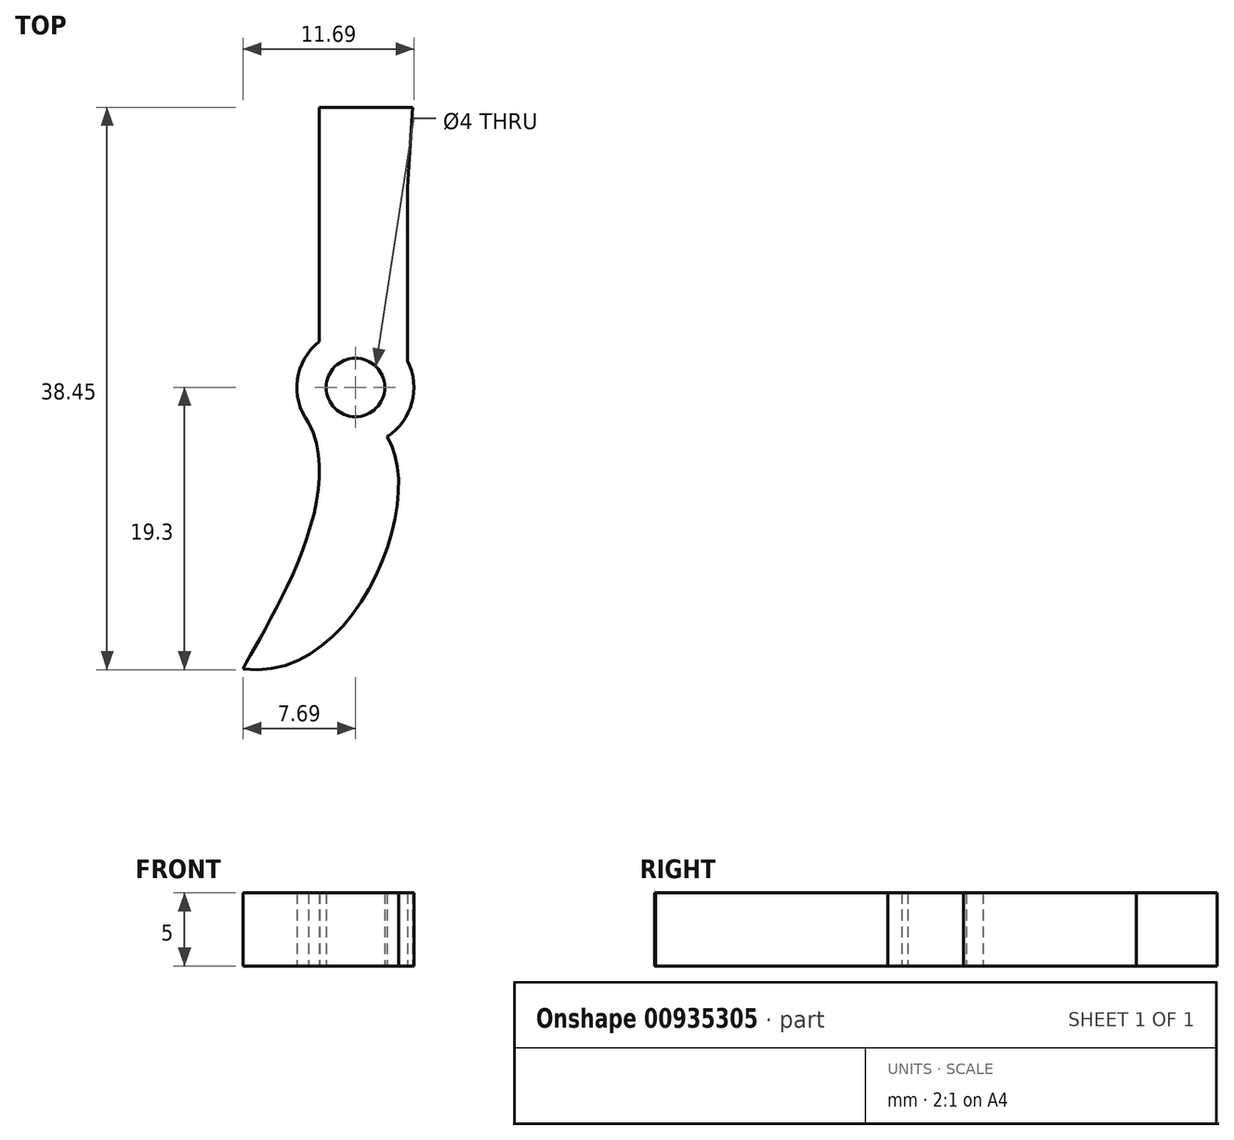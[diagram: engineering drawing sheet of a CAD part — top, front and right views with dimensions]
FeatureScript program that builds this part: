
annotation { "Feature Type Name" : "Feature", "Feature Type Description" : "" }
export const myFeature = defineFeature(function(context is Context, id is Id, definition is map)
    precondition{}
    {
        {
            var Q0;
            Q0=qCreatedBy(makeId("Top.planeOp"),FACE);
            var sketch = newSketch(context, id + "F0", { "sketchPlane" : qUnion([Q0])});
            skCircle(sketch, "E0", {"center": v(0, 0) * mm, "radius": 2 * mm});
            skCircle(sketch, "E1.0", {"center": v(0, 0) * mm, "radius": 4 * mm});
            skFitSpline(sketch, "E2", {"points": [v(-3.58, -1.78) * mm, v(-7.69, -19.23) * mm], "startDerivative": vector(10.75, -15.19) * mm, "endDerivative": vector(-5.28, -9.9) * mm});
            skFitSpline(sketch, "E3", {"points": [v(-7.69, -19.23) * mm, v(2.15, -3.37) * mm], "startDerivative": vector(23.06, -3.24) * mm, "endDerivative": vector(-8.43, 12.87) * mm});
            skLineSegment(sketch, "E4", {"start": v(-2.46, 3.15) * mm, "end": v(-2.46, 13.64) * mm});
            skLineSegment(sketch, "E5", {"start": v(3.57, 13.64) * mm, "end": v(3.57, 1.8) * mm});
            skLineSegment(sketch, "E6", {"start": v(-2.46, 13.64) * mm, "end": v(-2.46, 19.15) * mm});
            skLineSegment(sketch, "E7", {"start": v(-2.46, 19.15) * mm, "end": v(3.9, 19.15) * mm});
            skLineSegment(sketch, "E8", {"start": v(3.9, 19.15) * mm, "end": v(3.57, 13.64) * mm});
            skSolve(sketch);
        }
        {
            var Q0;
            Q0 = qSketchRegion(id + "F0", true);
            extrude(context, id + "F1", {"entities" : qUnion([Q0]), "depth" : 5 * mm, "offsetDistance" : 25 * mm});
        }
    });
